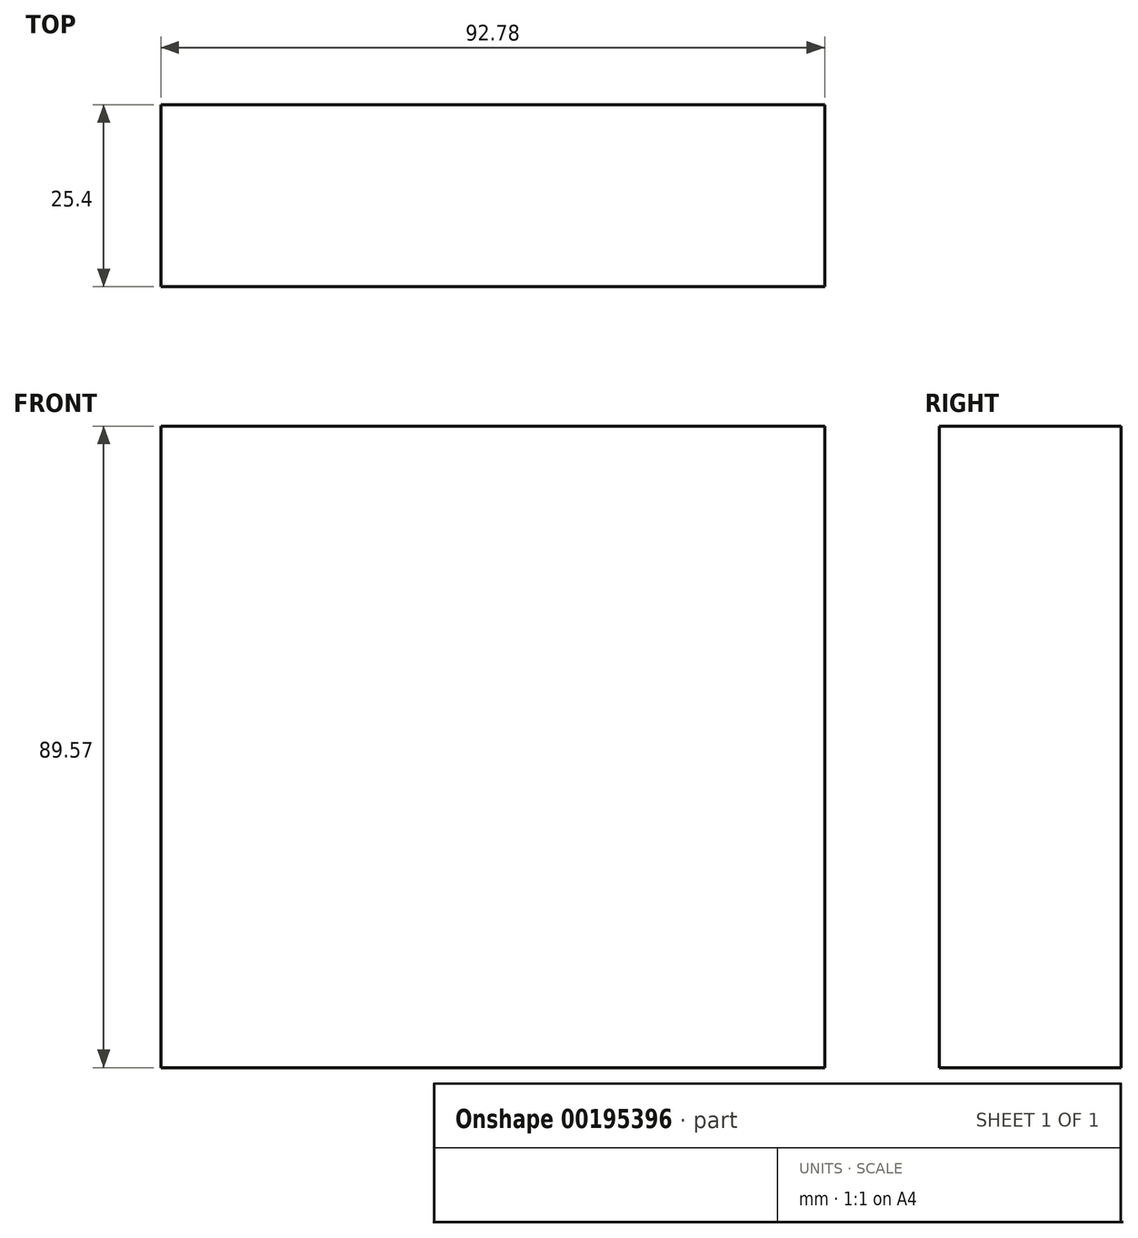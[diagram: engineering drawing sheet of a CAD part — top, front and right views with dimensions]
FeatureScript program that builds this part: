
annotation { "Feature Type Name" : "Feature", "Feature Type Description" : "" }
export const myFeature = defineFeature(function(context is Context, id is Id, definition is map)
    precondition{}
    {
        {
            var Q0;
            Q0=qCreatedBy(makeId("Front.planeOp"),FACE);
            var sketch = newSketch(context, id + "F0", { "sketchPlane" : qUnion([Q0])});
            skLineSegment(sketch, "E0.bottom", {"start": v(0, 0) * mm, "end": v(92.78, 0) * mm});
            skLineSegment(sketch, "E0.top", {"start": v(0, -89.57) * mm, "end": v(92.78, -89.57) * mm});
            skLineSegment(sketch, "E0.left", {"start": v(0, 0) * mm, "end": v(0, -89.57) * mm});
            skLineSegment(sketch, "E0.right", {"start": v(92.78, 0) * mm, "end": v(92.78, -89.57) * mm});
            skSolve(sketch);
        }
        {
            var Q0;
            Q0 = qSketchRegion(id + "F0", true);
            extrude(context, id + "F1", {"entities" : qUnion([Q0]), "depth" : 25.4 * mm});
        }
    });
